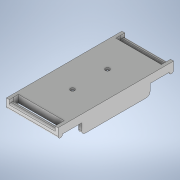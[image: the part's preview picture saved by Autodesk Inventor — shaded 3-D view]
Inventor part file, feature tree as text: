
AUTODESK INVENTOR PART (.ipt)
format: ipt  version: 2022 (Build 260153000, 153)  size: 217,088 bytes
history: native  units: mm
features: sketch x6, extrude x6, mirror x2, hole x1, fillet x1
ambient origin geometry x8: Origin, YZ Plane, XZ Plane, XY Plane, X Axis, Y Axis, Z Axis, Center Point
bodies: Solid1 (feature_tree)
feature tree (16):
  sketch  "Sketch1"  dims[d0=30.0mm d1=60.0mm]
  extrude  "Extrusion1"  Depth=60.0mm
  hole  "Hole1"  [1 undecoded]
  extrude  "Extrusion2"  Depth=18.5mm
  extrude  "Extrusion3"  Depth=34.0mm
  mirror  "Mirror1"
  extrude  "Extrusion4"  Depth=32.0mm
  extrude  "Extrusion5"  Depth=1.0mm
  extrude  "Extrusion6"  Depth=3.0mm TaperAngle=0.0deg
  mirror  "Mirror2"
  fillet  "Fillet2"  Radius=10.0mm
  sketch  "Sketch2"  dims[d2=30.0mm d3=15.0mm]
  sketch  "Sketch3"  dims[d4=23.0mm d5=18.5mm]
  sketch  "Sketch6"  dims[d6=2.0mm d7=0.0mm]
  sketch  "Sketch7"  dims[d8=2.8mm d9=6.0mm d10=5.0mm d11=0.5mm d12=90.0deg d13=8.0mm d14=20.594885mm d15=34.0mm]
  sketch  "Sketch8"  dims[d16=64.0mm d17=32.0mm d18=17.0mm d19=3.0mm d20=2.0mm d21=0.0mm d22=0.0mm d23=10.0mm d24=45.0mm d25=9.5mm d26=5.0mm d27=5.0mm d28=2.5mm d29=2.5mm d30=3.0mm d31=0.0mm d34=3.0mm d35=6.0mm d36=10.0mm d37=0.0mm d38=2.0mm d39=0.0mm d41=3.0mm d42=2.0mm d43=0.0mm d44=1.0mm]
note: 1 required parameter value undecoded (feature->parameter linkage not recoverable at this tier; creation-order binding heuristic only, values carry confidence <= 0.55)
